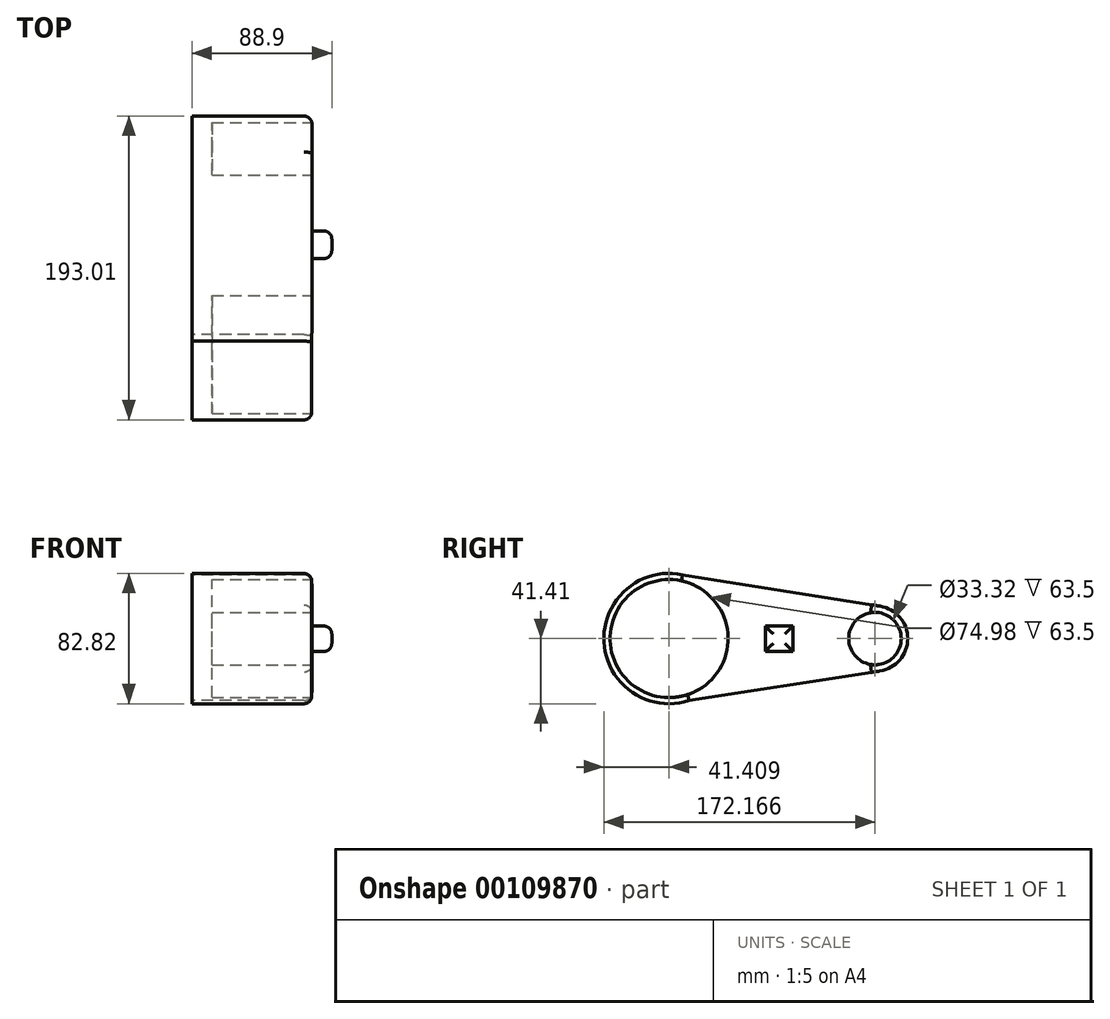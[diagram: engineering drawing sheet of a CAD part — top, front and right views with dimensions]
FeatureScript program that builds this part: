
annotation { "Feature Type Name" : "Feature", "Feature Type Description" : "" }
export const myFeature = defineFeature(function(context is Context, id is Id, definition is map)
    precondition{}
    {
        {
            var Q0;
            Q0=qCreatedBy(makeId("Right.planeOp"),FACE);
            var sketch = newSketch(context, id + "F0", { "sketchPlane" : qUnion([Q0])});
            skCircle(sketch, "E0", {"center": v(-69.47, 0) * mm, "radius": 41.4 * mm});
            skCircle(sketch, "E1", {"center": v(61.29, 0) * mm, "radius": 20.84 * mm});
            skLineSegment(sketch, "E2", {"start": v(-60.87, 40.5) * mm, "end": v(64.56, 20.58) * mm});
            skLineSegment(sketch, "E3", {"start": v(-56.75, -39.4) * mm, "end": v(64.48, -20.6) * mm});
            skSolve(sketch);
        }
        {
            var Q0;
            Q0 = qSketchRegion(id + "F0", true);
            extrude(context, id + "F1", {"entities" : qUnion([Q0]), "depth" : 76.2 * mm});
        }
        {
            var Q0;
            Q0=makeQuery(id+"F1.opExtrude","CAP_FACE",FACE,{"disambiguationData":[OSD([sQuery(id+"F0.wireOp",EDGE,"E0"),sQuery(id+"F0.wireOp",EDGE,"E1"),sQuery(id+"F0.wireOp",EDGE,"E2"),sQuery(id+"F0.wireOp",EDGE,"E3")])],"isStart":false});
            var sketch = newSketch(context, id + "F2", { "sketchPlane" : qUnion([Q0])});
            skCircle(sketch, "E4", {"center": v(-69.47, 0) * mm, "radius": 37.49 * mm});
            skCircle(sketch, "E5", {"center": v(61.29, 0) * mm, "radius": 16.66 * mm});
            skLineSegment(sketch, "E6.bottom", {"start": v(-8.36, 7.93) * mm, "end": v(9.16, 7.93) * mm});
            skLineSegment(sketch, "E6.top", {"start": v(-8.36, -8.17) * mm, "end": v(9.16, -8.17) * mm});
            skLineSegment(sketch, "E6.left", {"start": v(-8.36, 7.93) * mm, "end": v(-8.36, -8.17) * mm});
            skLineSegment(sketch, "E6.right", {"start": v(9.16, 7.93) * mm, "end": v(9.16, -8.17) * mm});
            skSolve(sketch);
        }
        {
            var Q0;
            Q0=makeQuery(id+"F2.imprint","IMPRINT",FACE,{"disambiguationData":[TD([[makeQuery(id+"F2.imprint","IMPRINT",EDGE,{"derivedFrom":sQuery(id+"F2.wireOp",EDGE,"E4")}),1.0]])]});
            var Q1;
            Q1=makeQuery(id+"F2.imprint","IMPRINT",FACE,{"disambiguationData":[TD([[makeQuery(id+"F2.imprint","IMPRINT",EDGE,{"derivedFrom":sQuery(id+"F2.wireOp",EDGE,"E5")}),1.0]])]});
            extrude(context, id + "F3", {"entities" : qUnion([Q0, Q1]), "operationType" : NewBodyOperationType.REMOVE, "oppositeDirection" : true, "depth" : 63.5 * mm});
        }
        {
            var Q0;
            Q0=makeQuery(id+"F2.imprint","IMPRINT",FACE,{"disambiguationData":[TD([[makeQuery(id+"F2.imprint","IMPRINT",EDGE,{"derivedFrom":sQuery(id+"F2.wireOp",EDGE,"E6.bottom")}),-1.0]])]});
            extrude(context, id + "F4", {"entities" : qUnion([Q0]), "operationType" : NewBodyOperationType.ADD, "depth" : 12.7 * mm});
        }
        {
            var Q0;
            Q0=makeQuery(id+"F1.opExtrude","CAP_EDGE",EDGE,{"disambiguationData":[OSD([sQuery(id+"F0.wireOp",EDGE,"E2")])],"isStart":false});
            var Q1;
            Q1=makeQuery(id+"F1.opExtrude","CAP_EDGE",EDGE,{"disambiguationData":[OSD([sQuery(id+"F0.wireOp",EDGE,"E0")])],"isStart":false});
            var Q2;
            Q2=makeQuery(id+"F1.opExtrude","CAP_EDGE",EDGE,{"disambiguationData":[OSD([sQuery(id+"F0.wireOp",EDGE,"E3")])],"isStart":false});
            var Q3;
            Q3=makeQuery(id+"F1.opExtrude","CAP_EDGE",EDGE,{"disambiguationData":[OSD([sQuery(id+"F0.wireOp",EDGE,"E1")])],"isStart":false});
            var Q4;
            Q4=makeQuery(id+"F3.boolean.opBoolean","COPY",EDGE,{"derivedFrom":makeQuery(id+"F3.opExtrude","CAP_EDGE",EDGE,{"disambiguationData":[OSD([sQuery(id+"F2.wireOp",EDGE,"E4")])],"isStart":true})});
            var Q5;
            Q5=makeQuery(id+"F3.boolean.opBoolean","COPY",EDGE,{"derivedFrom":makeQuery(id+"F3.opExtrude","CAP_EDGE",EDGE,{"disambiguationData":[OSD([sQuery(id+"F2.wireOp",EDGE,"E5")])],"isStart":true})});
            var Q6;
            Q6=makeQuery(id+"F4.opExtrude","CAP_EDGE",EDGE,{"disambiguationData":[OSD([sQuery(id+"F2.wireOp",EDGE,"E6.bottom")])],"isStart":false});
            var Q7;
            Q7=makeQuery(id+"F4.opExtrude","CAP_EDGE",EDGE,{"disambiguationData":[OSD([sQuery(id+"F2.wireOp",EDGE,"E6.left")])],"isStart":false});
            var Q8;
            Q8=makeQuery(id+"F4.opExtrude","CAP_EDGE",EDGE,{"disambiguationData":[OSD([sQuery(id+"F2.wireOp",EDGE,"E6.top")])],"isStart":false});
            var Q9;
            Q9=makeQuery(id+"F4.opExtrude","CAP_EDGE",EDGE,{"disambiguationData":[OSD([sQuery(id+"F2.wireOp",EDGE,"E6.right")])],"isStart":false});
            fillet(context, id + "F5", {"entities" : qUnion([Q0, Q1, Q2, Q3, Q4, Q5, Q6, Q7, Q8, Q9]), "radius" : 5.08 * mm, "tangentPropagation" : true, "allowEdgeOverflow" : false});
        }
    });
